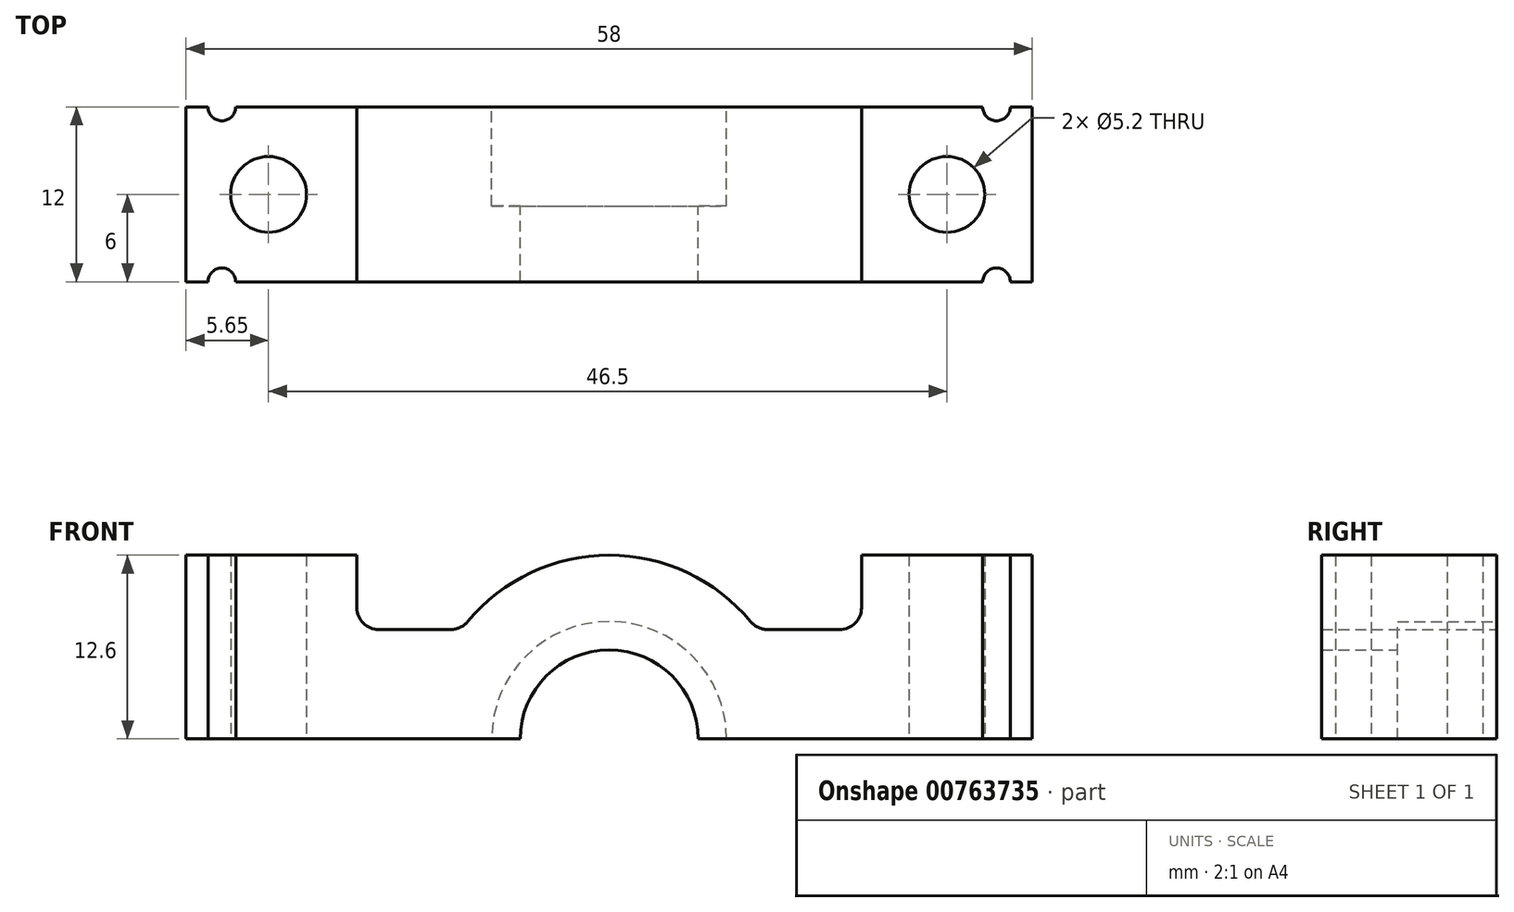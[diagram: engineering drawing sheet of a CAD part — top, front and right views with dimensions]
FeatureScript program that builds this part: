
annotation { "Feature Type Name" : "Feature", "Feature Type Description" : "" }
export const myFeature = defineFeature(function(context is Context, id is Id, definition is map)
    precondition{}
    {
        {
            var Q0;
            Q0=qCreatedBy(makeId("Top.planeOp"),FACE);
            var sketch = newSketch(context, id + "F0", { "sketchPlane" : qUnion([Q0])});
            skLineSegment(sketch, "E0.bottom", {"start": v(-29, 6) * mm, "end": v(-27.5, 6) * mm});
            skLineSegment(sketch, "E0.top", {"start": v(-29, -6) * mm, "end": v(-27.5, -6) * mm});
            skLineSegment(sketch, "E0.left", {"start": v(-29, 6) * mm, "end": v(-29, -6) * mm});
            skLineSegment(sketch, "E0.right", {"start": v(29, 6) * mm, "end": v(29, -6) * mm});
            skPoint(sketch, "E0.middle", {"position": v(0, 0) * mm});
            skCircle(sketch, "E1", {"center": v(-23.35, 0) * mm, "radius": 2.6 * mm});
            skCircle(sketch, "E2", {"center": v(23.15, 0) * mm, "radius": 2.6 * mm});
            skArc(sketch, "E3", {"start": v(-27.5, 6) * mm, "mid": v(-26.55, 5.05) * mm, "end": v(-25.6, 6) * mm});
            skLineSegment(sketch, "E4", {"start": v(-31.3, 0) * mm, "end": v(31.3, 0) * mm, "construction": true});
            skLineSegment(sketch, "E5", {"start": v(0, -6.22) * mm, "end": v(0, 9.07) * mm, "construction": true});
            skLineSegment(sketch, "E6.trimOffspring", {"start": v(-25.6, 6) * mm, "end": v(25.6, 6) * mm});
            skArc(sketch, "E7.MirrorCS", {"start": v(27.5, 6) * mm, "mid": v(26.55, 5.05) * mm, "end": v(25.6, 6) * mm});
            skLineSegment(sketch, "E8.MirrorCS", {"start": v(31.3, 0) * mm, "end": v(-31.3, 0) * mm, "construction": true});
            skArc(sketch, "E9.MirrorCS", {"start": v(-27.5, -6) * mm, "mid": v(-26.55, -5.05) * mm, "end": v(-25.6, -6) * mm});
            skArc(sketch, "E10.MirrorCS", {"start": v(27.5, -6) * mm, "mid": v(26.55, -5.05) * mm, "end": v(25.6, -6) * mm});
            skLineSegment(sketch, "E11.trimOffspring", {"start": v(-25.6, -6) * mm, "end": v(25.6, -6) * mm});
            skLineSegment(sketch, "E12.trimOffspring", {"start": v(27.5, -6) * mm, "end": v(29, -6) * mm});
            skLineSegment(sketch, "E13.trimOffspring", {"start": v(27.5, 6) * mm, "end": v(29, 6) * mm});
            skSolve(sketch);
        }
        {
            var Q0;
            Q0=makeQuery(id+"F0.imprint","IMPRINT",FACE,{"disambiguationData":[TD([[makeQuery(id+"F0.imprint","IMPRINT",EDGE,{"derivedFrom":sQuery(id+"F0.wireOp",EDGE,"E0.bottom")}),-1.0]])]});
            extrude(context, id + "F1", {"entities" : qUnion([Q0]), "depth" : 12.6 * mm, "offsetDistance" : 25 * mm});
        }
        {
            var Q0;
            Q0=makeQuery(id+"F1.opExtrude","SWEPT_FACE",FACE,{"disambiguationData":[OSD([sQuery(id+"F0.wireOp",EDGE,"E0.bottom")])]});
            var sketch = newSketch(context, id + "F2", { "sketchPlane" : qUnion([Q0])});
            skCircle(sketch, "E14", {"center": v(0, 0) * mm, "radius": 8.05 * mm});
            skCircle(sketch, "E15", {"center": v(0, 0) * mm, "radius": 6.1 * mm});
            skCircle(sketch, "E16", {"center": v(0, 0) * mm, "radius": 12.6 * mm});
            skLineSegment(sketch, "E17", {"start": v(-28.96, 6) * mm, "end": v(29, 6) * mm, "construction": true});
            skLineSegment(sketch, "E18", {"start": v(-11.08, 6) * mm, "end": v(-28.96, 6) * mm});
            skLineSegment(sketch, "E19", {"start": v(29, 6) * mm, "end": v(11.08, 6) * mm});
            skSolve(sketch);
        }
        {
            var Q0;
            Q0=makeQuery(id+"F2.imprint","IMPRINT",FACE,{"disambiguationData":[TD([[makeQuery(id+"F2.imprint","IMPRINT",EDGE,{"derivedFrom":sQuery(id+"F2.wireOp",EDGE,"E15")}),1.0]])]});
            extrude(context, id + "F3", {"entities" : qUnion([Q0]), "operationType" : NewBodyOperationType.REMOVE, "oppositeDirection" : true, "depth" : 13 * mm, "offsetDistance" : 25 * mm});
        }
        {
            var Q0;
            Q0=makeQuery(id+"F2.imprint","IMPRINT",FACE,{"disambiguationData":[TD([[makeQuery(id+"F2.imprint","IMPRINT",EDGE,{"derivedFrom":sQuery(id+"F2.wireOp",EDGE,"E14")}),1.0]])]});
            extrude(context, id + "F4", {"entities" : qUnion([Q0]), "operationType" : NewBodyOperationType.REMOVE, "oppositeDirection" : true, "depth" : 6.8 * mm, "offsetDistance" : 25 * mm});
        }
        {
            var Q0;
            Q0=makeQuery(id+"F1.opExtrude","SWEPT_BODY",BODY,{"disambiguationData":[OSD([sQuery(id+"F0.wireOp",EDGE,"E0.bottom"),sQuery(id+"F0.wireOp",EDGE,"E0.top"),sQuery(id+"F0.wireOp",EDGE,"E0.left"),sQuery(id+"F0.wireOp",EDGE,"E0.right"),sQuery(id+"F0.wireOp",EDGE,"E1"),sQuery(id+"F0.wireOp",EDGE,"E2"),sQuery(id+"F0.wireOp",EDGE,"E3"),sQuery(id+"F0.wireOp",EDGE,"E6.trimOffspring"),sQuery(id+"F0.wireOp",EDGE,"E7.MirrorCS"),sQuery(id+"F0.wireOp",EDGE,"E9.MirrorCS"),sQuery(id+"F0.wireOp",EDGE,"E10.MirrorCS"),sQuery(id+"F0.wireOp",EDGE,"E11.trimOffspring"),sQuery(id+"F0.wireOp",EDGE,"E12.trimOffspring"),sQuery(id+"F0.wireOp",EDGE,"E13.trimOffspring")])]});
            transform(context, id + "F5", {"entities" : qUnion([Q0]), "transformType" : TransformType.TRANSLATION_3D, "dx" : 0 * mm, "dy" : 0 * mm, "dz" : 0 * mm, "makeCopy" : true});
        }
        {
            var Q0;
            Q0=makeQuery(id+"F5.opPattern","COPY",BODY,{"derivedFrom":makeQuery(id+"F1.opExtrude","SWEPT_BODY",BODY,{"disambiguationData":[OSD([sQuery(id+"F0.wireOp",EDGE,"E0.bottom"),sQuery(id+"F0.wireOp",EDGE,"E0.top"),sQuery(id+"F0.wireOp",EDGE,"E0.left"),sQuery(id+"F0.wireOp",EDGE,"E0.right"),sQuery(id+"F0.wireOp",EDGE,"E1"),sQuery(id+"F0.wireOp",EDGE,"E2"),sQuery(id+"F0.wireOp",EDGE,"E3"),sQuery(id+"F0.wireOp",EDGE,"E6.trimOffspring"),sQuery(id+"F0.wireOp",EDGE,"E7.MirrorCS"),sQuery(id+"F0.wireOp",EDGE,"E9.MirrorCS"),sQuery(id+"F0.wireOp",EDGE,"E10.MirrorCS"),sQuery(id+"F0.wireOp",EDGE,"E11.trimOffspring"),sQuery(id+"F0.wireOp",EDGE,"E12.trimOffspring"),sQuery(id+"F0.wireOp",EDGE,"E13.trimOffspring")])]}),"instanceName":"1"});
            deleteBodies(context, id + "F6", {"entities" : qUnion([Q0])});
        }
        {
            var Q0;
            Q0=makeQuery(id+"F1.opExtrude","SWEPT_BODY",BODY,{"disambiguationData":[OSD([sQuery(id+"F0.wireOp",EDGE,"E0.bottom"),sQuery(id+"F0.wireOp",EDGE,"E0.top"),sQuery(id+"F0.wireOp",EDGE,"E0.left"),sQuery(id+"F0.wireOp",EDGE,"E0.right"),sQuery(id+"F0.wireOp",EDGE,"E1"),sQuery(id+"F0.wireOp",EDGE,"E2"),sQuery(id+"F0.wireOp",EDGE,"E3"),sQuery(id+"F0.wireOp",EDGE,"E6.trimOffspring"),sQuery(id+"F0.wireOp",EDGE,"E7.MirrorCS"),sQuery(id+"F0.wireOp",EDGE,"E9.MirrorCS"),sQuery(id+"F0.wireOp",EDGE,"E10.MirrorCS"),sQuery(id+"F0.wireOp",EDGE,"E11.trimOffspring"),sQuery(id+"F0.wireOp",EDGE,"E12.trimOffspring"),sQuery(id+"F0.wireOp",EDGE,"E13.trimOffspring")])]});
            var Q1;
            Q1=sQuery(id+"F0.wireOp",EDGE,"E5");
            transform(context, id + "F7", {"entities" : qUnion([Q0]), "transformType" : TransformType.ROTATION, "transformAxis" : qUnion([Q1]), "angle" : 180 * degree, "makeCopy" : true});
        }
        {
            var Q0;
            Q0=makeQuery(id+"F7.opPattern","COPY",BODY,{"derivedFrom":makeQuery(id+"F1.opExtrude","SWEPT_BODY",BODY,{"disambiguationData":[OSD([sQuery(id+"F0.wireOp",EDGE,"E0.bottom"),sQuery(id+"F0.wireOp",EDGE,"E0.top"),sQuery(id+"F0.wireOp",EDGE,"E0.left"),sQuery(id+"F0.wireOp",EDGE,"E0.right"),sQuery(id+"F0.wireOp",EDGE,"E1"),sQuery(id+"F0.wireOp",EDGE,"E2"),sQuery(id+"F0.wireOp",EDGE,"E3"),sQuery(id+"F0.wireOp",EDGE,"E6.trimOffspring"),sQuery(id+"F0.wireOp",EDGE,"E7.MirrorCS"),sQuery(id+"F0.wireOp",EDGE,"E9.MirrorCS"),sQuery(id+"F0.wireOp",EDGE,"E10.MirrorCS"),sQuery(id+"F0.wireOp",EDGE,"E11.trimOffspring"),sQuery(id+"F0.wireOp",EDGE,"E12.trimOffspring"),sQuery(id+"F0.wireOp",EDGE,"E13.trimOffspring")])]}),"instanceName":"1"});
            deleteBodies(context, id + "F8", {"entities" : qUnion([Q0])});
        }
        {
            var Q0;
            Q0=makeQuery(id+"F1.opExtrude","SWEPT_FACE",FACE,{"disambiguationData":[OSD([sQuery(id+"F0.wireOp",EDGE,"E6.trimOffspring")])]});
            var sketch = newSketch(context, id + "F9", { "sketchPlane" : qUnion([Q0])});
            skCircle(sketch, "E20", {"center": v(0, 0) * mm, "radius": 12.6 * mm});
            skLineSegment(sketch, "E21", {"start": v(-20.6, 32.7) * mm, "end": v(-20.6, -17.7) * mm, "construction": true});
            skLineSegment(sketch, "E22", {"start": v(-17.3, 12.6) * mm, "end": v(-17.3, 7.5) * mm});
            skLineSegment(sketch, "E23", {"start": v(-17.3, 7.5) * mm, "end": v(-10.12, 7.5) * mm});
            skPoint(sketch, "E24", {"position": v(-17.3, 7.5) * mm});
            skLineSegment(sketch, "E25", {"start": v(0, -8.48) * mm, "end": v(0, 23.34) * mm, "construction": true});
            skPoint(sketch, "E25.endSnap0", {"position": v(0, 8.05) * mm});
            skPoint(sketch, "E26", {"position": v(0, 12.6) * mm});
            skLineSegment(sketch, "E27.MirrorCS", {"start": v(17.3, 12.6) * mm, "end": v(17.3, 7.5) * mm});
            skLineSegment(sketch, "E28.MirrorCS", {"start": v(17.3, 7.5) * mm, "end": v(10.12, 7.5) * mm});
            skLineSegment(sketch, "E29", {"start": v(-17.3, 12.6) * mm, "end": v(17.3, 12.6) * mm});
            skSolve(sketch);
        }
        {
            var Q0;
            {var subQ4=sQuery(id+"F9.wireOp",EDGE,"E22");Q0=makeQuery(id+"F9.imprint","IMPRINT",FACE,{"disambiguationData":[TD([[makeQuery(id+"F9.imprint","IMPRINT",EDGE,{"derivedFrom":subQ4}),1.0]])]});}
            var Q1;
            {var subQ4=sQuery(id+"F9.wireOp",EDGE,"E27.MirrorCS");Q1=makeQuery(id+"F9.imprint","IMPRINT",FACE,{"disambiguationData":[TD([[makeQuery(id+"F9.imprint","IMPRINT",EDGE,{"derivedFrom":subQ4}),-1.0]])]});}
            extrude(context, id + "F10", {"entities" : qUnion([Q0, Q1]), "operationType" : NewBodyOperationType.REMOVE, "oppositeDirection" : true, "depth" : 13 * mm, "offsetDistance" : 25 * mm});
        }
        {
            var Q0;
            Q0=makeQuery(id+"F10.boolean.opBoolean","COPY",EDGE,{"derivedFrom":makeQuery(id+"F10.opExtrude","SWEPT_EDGE",EDGE,{"disambiguationData":[OSD([sQuery(id+"F9.wireOp",EDGE,"E22"),sQuery(id+"F9.wireOp",EDGE,"E23")])]})});
            var Q1;
            Q1=makeQuery(id+"F10.boolean.opBoolean","COPY",EDGE,{"derivedFrom":makeQuery(id+"F10.opExtrude","SWEPT_EDGE",EDGE,{"disambiguationData":[OSD([sQuery(id+"F9.wireOp",EDGE,"E20"),sQuery(id+"F9.wireOp",EDGE,"E23")])]})});
            var Q2;
            Q2=makeQuery(id+"F10.boolean.opBoolean","COPY",EDGE,{"derivedFrom":makeQuery(id+"F10.opExtrude","SWEPT_EDGE",EDGE,{"disambiguationData":[OSD([sQuery(id+"F9.wireOp",EDGE,"E20"),sQuery(id+"F9.wireOp",EDGE,"E28.MirrorCS")])]})});
            var Q3;
            Q3=makeQuery(id+"F10.boolean.opBoolean","COPY",EDGE,{"derivedFrom":makeQuery(id+"F10.opExtrude","SWEPT_EDGE",EDGE,{"disambiguationData":[OSD([sQuery(id+"F9.wireOp",EDGE,"E27.MirrorCS"),sQuery(id+"F9.wireOp",EDGE,"E28.MirrorCS")])]})});
            fillet(context, id + "F11", {"entities" : qUnion([Q0, Q1, Q2, Q3]), "radius" : 1.5 * mm, "tangentPropagation" : true, "allowEdgeOverflow" : false});
        }
    });
